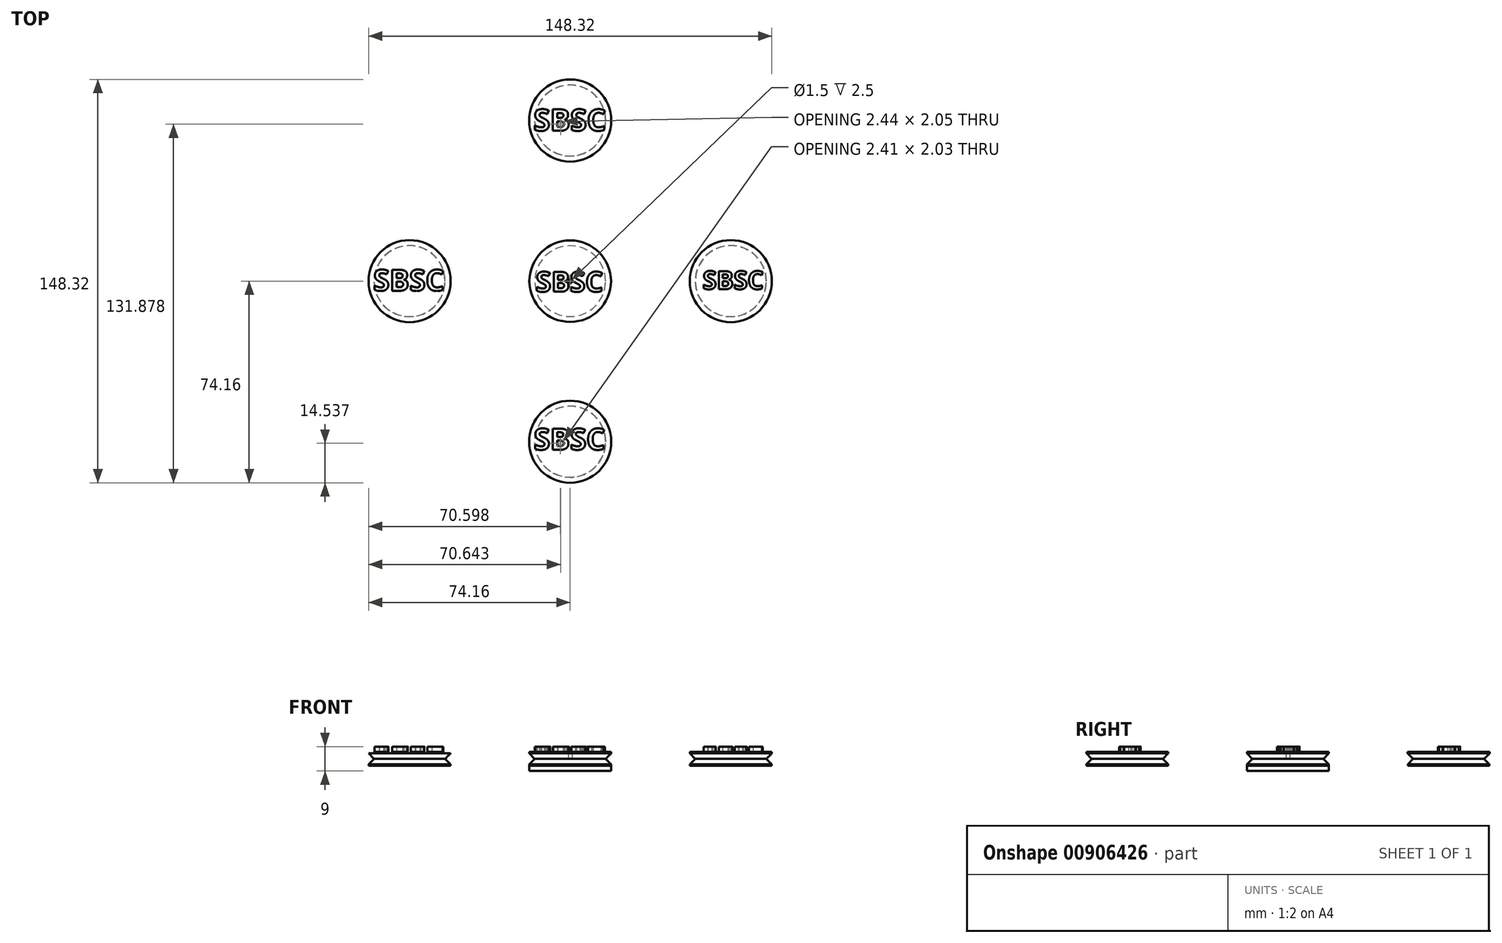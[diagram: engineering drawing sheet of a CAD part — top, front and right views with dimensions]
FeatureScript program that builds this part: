
annotation { "Feature Type Name" : "Feature", "Feature Type Description" : "" }
export const myFeature = defineFeature(function(context is Context, id is Id, definition is map)
    precondition{}
    {
        {
            var Q0;
            Q0=qCreatedBy(makeId("Top.planeOp"),FACE);
            var sketch = newSketch(context, id + "F0", { "sketchPlane" : qUnion([Q0])});
            skCircle(sketch, "E0", {"center": v(0, 0) * mm, "radius": 15 * mm});
            skCircle(sketch, "E1", {"center": v(59.06, 0) * mm, "radius": 15 * mm});
            skCircle(sketch, "E2", {"center": v(0, 59.06) * mm, "radius": 15 * mm});
            skCircle(sketch, "E3", {"center": v(-59.06, 0) * mm, "radius": 15 * mm});
            skCircle(sketch, "E4", {"center": v(0, -59.06) * mm, "radius": 15 * mm});
            skCircle(sketch, "E5", {"center": v(0, 0) * mm, "radius": 59.06 * mm, "construction": true});
            skSolve(sketch);
        }
        {
            var Q0;
            Q0=makeQuery(id+"F0.imprint","IMPRINT",FACE,{"disambiguationData":[TD([[makeQuery(id+"F0.imprint","IMPRINT",EDGE,{"derivedFrom":sQuery(id+"F0.wireOp",EDGE,"E0")}),1.0]])]});
            var Q1;
            Q1=makeQuery(id+"F0.imprint","IMPRINT",FACE,{"disambiguationData":[TD([[makeQuery(id+"F0.imprint","IMPRINT",EDGE,{"derivedFrom":sQuery(id+"F0.wireOp",EDGE,"E3")}),1.0]])]});
            var Q2;
            Q2=makeQuery(id+"F0.imprint","IMPRINT",FACE,{"disambiguationData":[TD([[makeQuery(id+"F0.imprint","IMPRINT",EDGE,{"derivedFrom":sQuery(id+"F0.wireOp",EDGE,"E2")}),1.0]])]});
            var Q3;
            Q3=makeQuery(id+"F0.imprint","IMPRINT",FACE,{"disambiguationData":[TD([[makeQuery(id+"F0.imprint","IMPRINT",EDGE,{"derivedFrom":sQuery(id+"F0.wireOp",EDGE,"E4")}),1.0]])]});
            var Q4;
            Q4=makeQuery(id+"F0.imprint","IMPRINT",FACE,{"disambiguationData":[TD([[makeQuery(id+"F0.imprint","IMPRINT",EDGE,{"derivedFrom":sQuery(id+"F0.wireOp",EDGE,"E1")}),1.0]])]});
            extrude(context, id + "F1", {"entities" : qUnion([Q0, Q1, Q2, Q3, Q4]), "depth" : 2.5 * mm, "offsetDistance" : 25 * mm});
        }
        {
            var Q0;
            Q0=makeQuery(id+"F1.opExtrude","CAP_FACE",FACE,{"disambiguationData":[OSD([sQuery(id+"F0.wireOp",EDGE,"E0")])],"isStart":false});
            var sketch = newSketch(context, id + "F2", { "sketchPlane" : qUnion([Q0])});
            skCircle(sketch, "E6", {"center": v(0, 0) * mm, "radius": 0.75 * mm});
            skSolve(sketch);
        }
        {
            var Q0;
            Q0=makeQuery(id+"F1.opExtrude","CAP_EDGE",EDGE,{"disambiguationData":[OSD([sQuery(id+"F0.wireOp",EDGE,"E0")])],"isStart":false});
            var Q1;
            Q1=makeQuery(id+"F1.opExtrude","CAP_EDGE",EDGE,{"disambiguationData":[OSD([sQuery(id+"F0.wireOp",EDGE,"E1")])],"isStart":false});
            var Q2;
            Q2=makeQuery(id+"F1.opExtrude","CAP_EDGE",EDGE,{"disambiguationData":[OSD([sQuery(id+"F0.wireOp",EDGE,"E4")])],"isStart":false});
            var Q3;
            Q3=makeQuery(id+"F1.opExtrude","CAP_EDGE",EDGE,{"disambiguationData":[OSD([sQuery(id+"F0.wireOp",EDGE,"E3")])],"isStart":false});
            var Q4;
            Q4=makeQuery(id+"F1.opExtrude","CAP_EDGE",EDGE,{"disambiguationData":[OSD([sQuery(id+"F0.wireOp",EDGE,"E2")])],"isStart":false});
            chamfer(context, id + "F3", {"entities" : qUnion([Q0, Q1, Q2, Q3, Q4]), "width" : 2 * mm, "tangentPropagation" : true});
        }
        {
            var Q0;
            Q0=makeQuery(id+"F2.imprint","IMPRINT",FACE,{"disambiguationData":[TD([[makeQuery(id+"F2.imprint","IMPRINT",EDGE,{"derivedFrom":sQuery(id+"F2.wireOp",EDGE,"E6")}),-1.0]])]});
            extrude(context, id + "F4", {"entities" : qUnion([Q0]), "operationType" : NewBodyOperationType.ADD, "depth" : 2.5 * mm, "offsetDistance" : 25 * mm});
        }
        {
            var Q0;
            Q0=makeQuery(id+"F4.opExtrude","CAP_EDGE",EDGE,{"disambiguationData":[OSD([sQuery(id+"F0.wireOp",EDGE,"E0")])],"isStart":true});
            chamfer(context, id + "F5", {"entities" : qUnion([Q0]), "width" : 2 * mm, "tangentPropagation" : true});
        }
        {
            var Q0;
            Q0=makeQuery(id+"F1.opExtrude","CAP_FACE",FACE,{"disambiguationData":[OSD([sQuery(id+"F0.wireOp",EDGE,"E2")])],"isStart":false});
            var sketch = newSketch(context, id + "F6", { "sketchPlane" : qUnion([Q0])});
            skCircle(sketch, "E7", {"center": v(0, 59.06) * mm, "radius": 15.1 * mm});
            skSolve(sketch);
        }
        {
            var Q0;
            Q0=makeQuery(id+"F6.imprint","IMPRINT",FACE,{"disambiguationData":[TD([[makeQuery(id+"F6.imprint","IMPRINT",EDGE,{"derivedFrom":sQuery(id+"F6.wireOp",EDGE,"E7")}),1.0]])]});
            var Q1;
            {var subQ0=sQuery(id+"F0.wireOp",EDGE,"E2");Q1=makeQuery(id+"F6.imprint","IMPRINT",FACE,{"disambiguationData":[TD([[makeQuery(id+"F6.imprint","IMPRINT",EDGE,{"derivedFrom":makeQuery(id+"F3.opChamfer","BLEND_EDGE",EDGE,{"blendedFrom":[makeQuery(id+"F1.opExtrude","CAP_EDGE",EDGE,{"disambiguationData":[OSD([subQ0])],"isStart":false}),makeQuery(id+"F1.opExtrude","CAP_FACE",FACE,{"disambiguationData":[OSD([subQ0])],"isStart":false})],"blendedInto":[makeQuery(id+"F1.opExtrude","CAP_FACE",FACE,{"disambiguationData":[OSD([subQ0])],"isStart":false})]})}),1.0]])]});}
            extrude(context, id + "F7", {"entities" : qUnion([Q0, Q1]), "operationType" : NewBodyOperationType.ADD, "depth" : 2.5 * mm, "offsetDistance" : 25 * mm});
        }
        {
            var Q0;
            Q0=makeQuery(id+"F7.opExtrude","CAP_EDGE",EDGE,{"disambiguationData":[OSD([sQuery(id+"F6.wireOp",EDGE,"E7")])],"isStart":true});
            chamfer(context, id + "F8", {"entities" : qUnion([Q0]), "width" : 2 * mm, "tangentPropagation" : true});
        }
        {
            var Q0;
            Q0=makeQuery(id+"F1.opExtrude","CAP_FACE",FACE,{"disambiguationData":[OSD([sQuery(id+"F0.wireOp",EDGE,"E3")])],"isStart":false});
            var sketch = newSketch(context, id + "F9", { "sketchPlane" : qUnion([Q0])});
            skCircle(sketch, "E8", {"center": v(-59.06, 0) * mm, "radius": 15.1 * mm});
            skSolve(sketch);
        }
        {
            var Q0;
            Q0=makeQuery(id+"F9.imprint","IMPRINT",FACE,{"disambiguationData":[TD([[makeQuery(id+"F9.imprint","IMPRINT",EDGE,{"derivedFrom":sQuery(id+"F9.wireOp",EDGE,"E8")}),1.0]])]});
            var Q1;
            {var subQ0=sQuery(id+"F0.wireOp",EDGE,"E3");Q1=makeQuery(id+"F9.imprint","IMPRINT",FACE,{"disambiguationData":[TD([[makeQuery(id+"F9.imprint","IMPRINT",EDGE,{"derivedFrom":makeQuery(id+"F3.opChamfer","BLEND_EDGE",EDGE,{"blendedFrom":[makeQuery(id+"F1.opExtrude","CAP_EDGE",EDGE,{"disambiguationData":[OSD([subQ0])],"isStart":false}),makeQuery(id+"F1.opExtrude","CAP_FACE",FACE,{"disambiguationData":[OSD([subQ0])],"isStart":false})],"blendedInto":[makeQuery(id+"F1.opExtrude","CAP_FACE",FACE,{"disambiguationData":[OSD([subQ0])],"isStart":false})]})}),1.0]])]});}
            extrude(context, id + "F10", {"entities" : qUnion([Q0, Q1]), "operationType" : NewBodyOperationType.ADD, "depth" : 2 * mm, "offsetDistance" : 25 * mm});
        }
        {
            var Q0;
            Q0=makeQuery(id+"F10.opExtrude","CAP_EDGE",EDGE,{"disambiguationData":[OSD([sQuery(id+"F9.wireOp",EDGE,"E8")])],"isStart":true});
            chamfer(context, id + "F11", {"entities" : qUnion([Q0]), "width" : 2 * mm, "tangentPropagation" : true});
        }
        {
            var Q0;
            Q0=makeQuery(id+"F1.opExtrude","CAP_FACE",FACE,{"disambiguationData":[OSD([sQuery(id+"F0.wireOp",EDGE,"E4")])],"isStart":false});
            var sketch = newSketch(context, id + "F12", { "sketchPlane" : qUnion([Q0])});
            skCircle(sketch, "E9", {"center": v(0, -59.06) * mm, "radius": 15.1 * mm});
            skSolve(sketch);
        }
        {
            var Q0;
            Q0 = qSketchRegion(id + "F12", true);
            extrude(context, id + "F13", {"entities" : qUnion([Q0]), "operationType" : NewBodyOperationType.ADD, "depth" : 2.5 * mm, "offsetDistance" : 25 * mm});
        }
        {
            var Q0;
            Q0=makeQuery(id+"F13.opExtrude","CAP_EDGE",EDGE,{"disambiguationData":[OSD([sQuery(id+"F12.wireOp",EDGE,"E9")])],"isStart":true});
            chamfer(context, id + "F14", {"entities" : qUnion([Q0]), "width" : 2 * mm, "tangentPropagation" : true});
        }
        {
            var Q0;
            Q0=makeQuery(id+"F1.opExtrude","CAP_FACE",FACE,{"disambiguationData":[OSD([sQuery(id+"F0.wireOp",EDGE,"E1")])],"isStart":false});
            var sketch = newSketch(context, id + "F15", { "sketchPlane" : qUnion([Q0])});
            skCircle(sketch, "E10", {"center": v(59.06, 0) * mm, "radius": 15.1 * mm});
            skSolve(sketch);
        }
        {
            var Q0;
            Q0 = qSketchRegion(id + "F15", true);
            extrude(context, id + "F16", {"entities" : qUnion([Q0]), "operationType" : NewBodyOperationType.ADD, "depth" : 2.5 * mm, "offsetDistance" : 25 * mm});
        }
        {
            var Q0;
            Q0=makeQuery(id+"F16.opExtrude","CAP_EDGE",EDGE,{"disambiguationData":[OSD([sQuery(id+"F15.wireOp",EDGE,"E10")])],"isStart":true});
            chamfer(context, id + "F17", {"entities" : qUnion([Q0]), "width" : 2 * mm, "tangentPropagation" : true});
        }
        {
            var Q0;
            Q0=makeQuery(id+"F7.opExtrude","CAP_FACE",FACE,{"disambiguationData":[OSD([sQuery(id+"F6.wireOp",EDGE,"E7")])],"isStart":false});
            var sketch = newSketch(context, id + "F18", { "sketchPlane" : qUnion([Q0])});
            skText(sketch, "E11", { "text": "SBSC", "fontName": "OpenSans-Bold.ttf"});
            const initialGuessF18  = {"E11": [-0.01266, -0.0039, 1, 0, 0.0074]};
            skSetInitialGuess(sketch, initialGuessF18);
            skSolve(sketch);
        }
        {
            var Q0;
            Q0=makeQuery(id+"F16.opExtrude","CAP_FACE",FACE,{"disambiguationData":[OSD([sQuery(id+"F15.wireOp",EDGE,"E10")])],"isStart":false});
            var sketch = newSketch(context, id + "F19", { "sketchPlane" : qUnion([Q0])});
            skText(sketch, "E12", { "text": "SBSC", "fontName": "OpenSans-Bold.ttf"});
            skText(sketch, "E13", { "text": "SBSC\n", "fontName": "OpenSans-Bold.ttf"});
            skText(sketch, "E14", { "text": "SBSC", "fontName": "OpenSans-Bold.ttf"});
            skText(sketch, "E15", { "text": "SBSC", "fontName": "OpenSans-Bold.ttf"});
            const initialGuessF19  = {"E12": [0.04872, -0.00295, 1, 0, 0.0067], "E13": [-0.0134, -0.062, 1, 0, 0.00785], "E14": [-0.07241, -0.00354, 1, 0, 0.0078], "E15": [-0.01348, 0.05531, 1, 0, 0.00795]};
            skSetInitialGuess(sketch, initialGuessF19);
            skSolve(sketch);
        }
        {
            var Q0;
            Q0 = qSketchRegion(id + "F19", true);
            var Q1;
            Q1 = qSketchRegion(id + "F18", true);
            extrude(context, id + "F20", {"entities" : qUnion([Q0, Q1]), "depth" : 2 * mm, "offsetDistance" : 25 * mm});
        }
        {
            var Q0;
            Q0=makeQuery(id+"F0.imprint","IMPRINT",FACE,{"disambiguationData":[TD([[makeQuery(id+"F0.imprint","IMPRINT",EDGE,{"derivedFrom":sQuery(id+"F0.wireOp",EDGE,"E0")}),1.0]])]});
            extrude(context, id + "F21", {"entities" : qUnion([Q0]), "operationType" : NewBodyOperationType.ADD, "oppositeDirection" : true, "depth" : 2 * mm, "offsetDistance" : 25 * mm});
        }
    });
